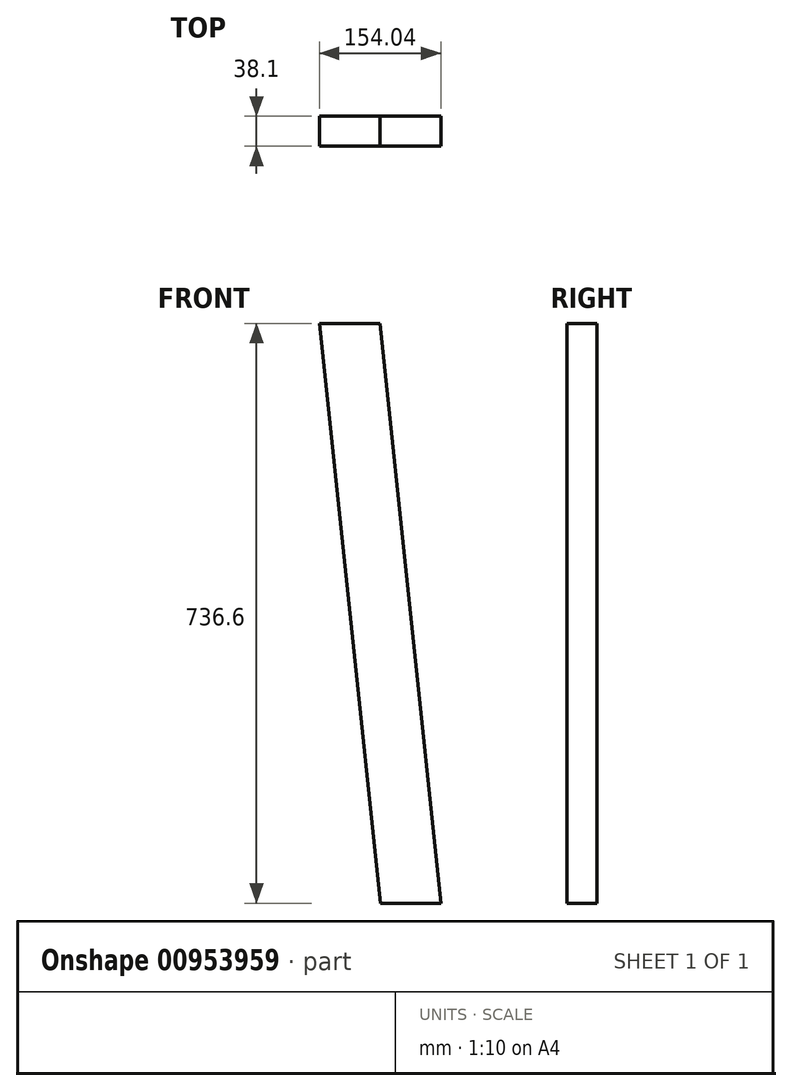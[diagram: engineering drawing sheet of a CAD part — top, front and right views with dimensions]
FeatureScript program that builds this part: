
annotation { "Feature Type Name" : "Feature", "Feature Type Description" : "" }
export const myFeature = defineFeature(function(context is Context, id is Id, definition is map)
    precondition{}
    {
        {
            var Q0;
            Q0=qCreatedBy(makeId("Front.planeOp"),FACE);
            var sketch = newSketch(context, id + "F0", { "sketchPlane" : qUnion([Q0])});
            skLineSegment(sketch, "E0", {"start": v(0, 0) * mm, "end": v(76.62, 0) * mm});
            skLineSegment(sketch, "E1", {"start": v(76.62, 0) * mm, "end": v(154.04, -736.6) * mm});
            skLineSegment(sketch, "E2", {"start": v(154.04, -736.6) * mm, "end": v(77.42, -736.6) * mm});
            skLineSegment(sketch, "E3", {"start": v(77.42, -736.6) * mm, "end": v(0, 0) * mm});
            skLineSegment(sketch, "E4", {"start": v(76.62, 0) * mm, "end": v(0.84, -7.97) * mm, "construction": true});
            skSolve(sketch);
        }
        {
            var Q0;
            Q0=makeQuery(id+"F0.imprint","IMPRINT",FACE,{"disambiguationData":[TD([[makeQuery(id+"F0.imprint","IMPRINT",EDGE,{"derivedFrom":sQuery(id+"F0.wireOp",EDGE,"E0")}),-1.0]])]});
            extrude(context, id + "F1", {"entities" : qUnion([Q0]), "depth" : 38.1 * mm, "offsetDistance" : 25.4 * mm});
        }
    });
